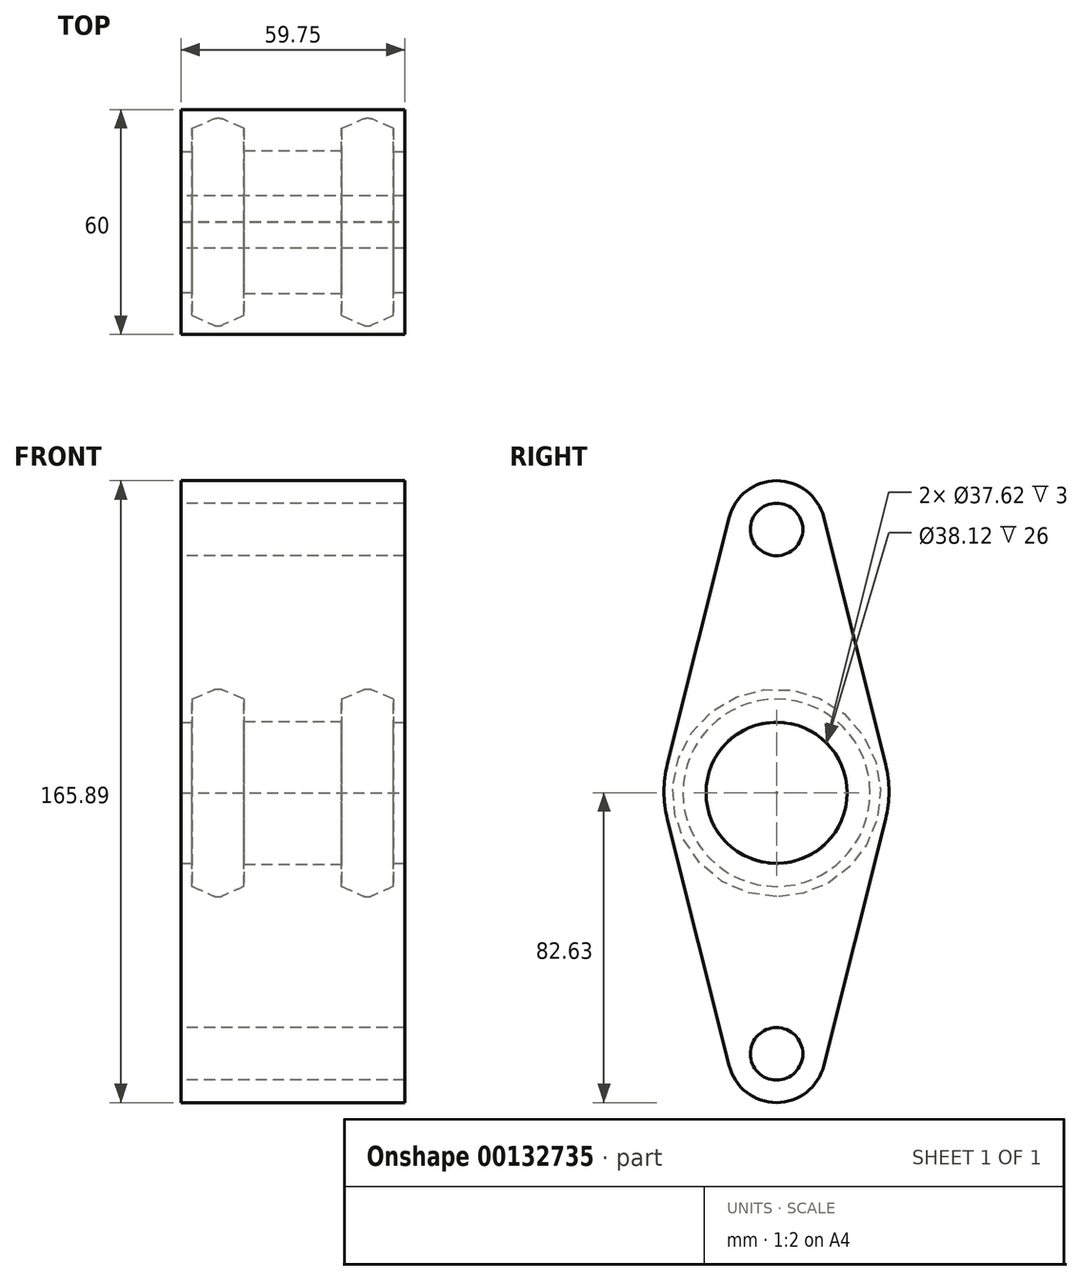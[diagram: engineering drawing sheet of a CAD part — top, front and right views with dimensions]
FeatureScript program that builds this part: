
annotation { "Feature Type Name" : "Feature", "Feature Type Description" : "" }
export const myFeature = defineFeature(function(context is Context, id is Id, definition is map)
    precondition{}
    {
        {
            var Q0;
            Q0=qCreatedBy(makeId("Front.planeOp"),FACE);
            var sketch = newSketch(context, id + "F0", { "sketchPlane" : qUnion([Q0])});
            skLineSegment(sketch, "E0", {"start": v(-26.44, 0) * mm, "end": v(-23.44, 0) * mm});
            skLineSegment(sketch, "E1", {"start": v(-23.44, 0) * mm, "end": v(-23.44, 6.15) * mm});
            skLineSegment(sketch, "E2", {"start": v(-23.44, 6.15) * mm, "end": v(-17.71, 8.67) * mm});
            skLineSegment(sketch, "E3", {"start": v(-11.46, 0) * mm, "end": v(-11.46, 0) * mm});
            skLineSegment(sketch, "E4", {"start": v(-9.57, 6.15) * mm, "end": v(-9.57, 0.25) * mm});
            skLineSegment(sketch, "E5", {"start": v(-9.57, 0.25) * mm, "end": v(3.43, 0.25) * mm});
            skLineSegment(sketch, "E6.MirrorCS", {"start": v(33.3, 0) * mm, "end": v(30.3, 0) * mm});
            skLineSegment(sketch, "E7.MirrorCS", {"start": v(30.3, 0) * mm, "end": v(30.3, 6.15) * mm});
            skLineSegment(sketch, "E8.MirrorCS", {"start": v(30.3, 6.15) * mm, "end": v(24.58, 8.67) * mm});
            skLineSegment(sketch, "E9.MirrorCS", {"start": v(22.16, 8.67) * mm, "end": v(16.43, 6.15) * mm});
            skLineSegment(sketch, "E10.MirrorCS", {"start": v(16.43, 6.15) * mm, "end": v(16.43, 0.25) * mm});
            skLineSegment(sketch, "E11.MirrorCS", {"start": v(16.43, 0.25) * mm, "end": v(3.43, 0.25) * mm});
            skLineSegment(sketch, "E12.MirrorCS", {"start": v(-23.44, -37.5) * mm, "end": v(-23.44, -43.65) * mm});
            skLineSegment(sketch, "E13.MirrorCS", {"start": v(-23.44, -43.65) * mm, "end": v(-17.71, -46.17) * mm});
            skLineSegment(sketch, "E14.MirrorCS", {"start": v(-15.3, -46.17) * mm, "end": v(-9.57, -43.65) * mm});
            skLineSegment(sketch, "E15.MirrorCS", {"start": v(-9.57, -43.65) * mm, "end": v(-9.57, -37.75) * mm});
            skLineSegment(sketch, "E16.MirrorCS", {"start": v(-9.57, -37.75) * mm, "end": v(3.43, -37.75) * mm});
            skLineSegment(sketch, "E17.MirrorCS", {"start": v(16.43, -37.75) * mm, "end": v(3.43, -37.75) * mm});
            skLineSegment(sketch, "E18.MirrorCS", {"start": v(16.43, -43.65) * mm, "end": v(16.43, -37.75) * mm});
            skLineSegment(sketch, "E19.MirrorCS", {"start": v(22.16, -46.17) * mm, "end": v(16.43, -43.65) * mm});
            skLineSegment(sketch, "E20.MirrorCS", {"start": v(30.3, -43.65) * mm, "end": v(24.58, -46.17) * mm});
            skLineSegment(sketch, "E21.MirrorCS", {"start": v(30.3, -37.5) * mm, "end": v(30.3, -43.65) * mm});
            skPoint(sketch, "E22.second.point", {"position": v(-16.45, 9.18) * mm});
            skPoint(sketch, "E22.third.point", {"position": v(-16.5, 4.16) * mm});
            skArc(sketch, "E23", {"start": v(-15.3, 8.67) * mm, "mid": v(-16.5, 8.93) * mm, "end": v(-17.71, 8.67) * mm});
            skArc(sketch, "E24.MirrorCS", {"start": v(-15.3, -46.17) * mm, "mid": v(-16.5, -46.43) * mm, "end": v(-17.71, -46.17) * mm});
            skArc(sketch, "E25.MirrorCS", {"start": v(22.16, 8.67) * mm, "mid": v(23.37, 8.93) * mm, "end": v(24.58, 8.67) * mm});
            skArc(sketch, "E26.MirrorCS", {"start": v(22.16, -46.17) * mm, "mid": v(23.37, -46.43) * mm, "end": v(24.58, -46.17) * mm});
            skLineSegment(sketch, "E27.trimOffspring", {"start": v(-15.3, 8.67) * mm, "end": v(-9.57, 6.15) * mm});
            skPoint(sketch, "E28.start.orphan", {"position": v(-16.5, 9.2) * mm});
            skPoint(sketch, "E29.orphan", {"position": v(23.37, 9.2) * mm});
            skPoint(sketch, "E30.orphan", {"position": v(23.37, -46.7) * mm});
            skPoint(sketch, "E31.orphan", {"position": v(-16.5, -46.7) * mm});
            skLineSegment(sketch, "E32", {"start": v(-26.44, -37.5) * mm, "end": v(-23.44, -37.5) * mm});
            skLineSegment(sketch, "E33", {"start": v(30.3, -37.5) * mm, "end": v(33.3, -37.5) * mm});
            skLineSegment(sketch, "E34", {"start": v(-26.44, 0) * mm, "end": v(-26.44, -18.75) * mm});
            skLineSegment(sketch, "E35", {"start": v(33.3, 0) * mm, "end": v(33.3, -18.75) * mm});
            skLineSegment(sketch, "E36", {"start": v(-26.44, -18.75) * mm, "end": v(33.3, -18.75) * mm});
            skSolve(sketch);
        }
        {
            var Q0;
            Q0=qCreatedBy(makeId("Front.planeOp"),FACE);
            var sketch = newSketch(context, id + "F1", { "sketchPlane" : qUnion([Q0])});
            skLineSegment(sketch, "E37", {"start": v(42.19, -18.81) * mm, "end": v(-37.88, -18.81) * mm});
            skSolve(sketch);
        }
        {
            var Q0;
            Q0=qCreatedBy(makeId("Right.planeOp"),FACE);
            var sketch = newSketch(context, id + "F2", { "sketchPlane" : qUnion([Q0])});
            skArc(sketch, "E38", {"start": v(-29.12, -11.19) * mm, "mid": v(-30.03, -18.5) * mm, "end": v(-29.12, -25.8) * mm});
            skPoint(sketch, "E39.0", {"position": v(0, -37.31) * mm});
            skArc(sketch, "E40", {"start": v(12.61, 54.6) * mm, "mid": v(0, 64.45) * mm, "end": v(-12.6, 54.62) * mm});
            skLineSegment(sketch, "E41", {"start": v(-29.12, -11.19) * mm, "end": v(-12.6, 54.62) * mm});
            skLineSegment(sketch, "E42", {"start": v(12.61, 54.6) * mm, "end": v(29.08, -11.21) * mm});
            skLineSegment(sketch, "E43", {"start": v(-33.72, -18.5) * mm, "end": v(35.57, -18.5) * mm});
            skCircle(sketch, "E44", {"center": v(0, 51.45) * mm, "radius": 7 * mm});
            skLineSegment(sketch, "E45.MirrorCS", {"start": v(-29.12, -25.8) * mm, "end": v(-12.6, -91.6) * mm});
            skArc(sketch, "E46.MirrorCS", {"start": v(12.61, -91.6) * mm, "mid": v(0, -101.44) * mm, "end": v(-12.6, -91.6) * mm});
            skLineSegment(sketch, "E47.MirrorCS", {"start": v(12.61, -91.6) * mm, "end": v(29.08, -25.77) * mm});
            skCircle(sketch, "E48.MirrorC", {"center": v(0, -88.44) * mm, "radius": 7 * mm});
            skArc(sketch, "E49.trimOffspring", {"start": v(29.08, -25.77) * mm, "mid": v(29.97, -18.5) * mm, "end": v(29.08, -11.21) * mm});
            skSolve(sketch);
        }
        {
            var Q0;
            Q0=makeQuery(id+"F0.imprint","IMPRINT",FACE,{"disambiguationData":[TD([[makeQuery(id+"F0.imprint","IMPRINT",EDGE,{"derivedFrom":sQuery(id+"F0.wireOp",EDGE,"E0")}),-1.0]])]});
            var Q1;
            Q1=sQuery(id+"F1.wireOp",EDGE,"E37");
            revolve(context, id + "F3", {"entities" : qUnion([Q0]), "axis" : qUnion([Q1]), "revolveType" : RevolveType.FULL});
        }
        {
            var Q0;
            Q0=makeQuery(id+"F2.imprint","IMPRINT",FACE,{"disambiguationData":[TD([[makeQuery(id+"F2.imprint","IMPRINT",EDGE,{"derivedFrom":sQuery(id+"F2.wireOp",EDGE,"E40")}),1.0]])]});
            var Q1;
            {var subQ0=sQuery(id+"F2.wireOp",EDGE,"E43");var subQ1=sQuery(id+"F2.wireOp",EDGE,"E38");var subQ2=makeQuery(id+"F2.imprint","INTERSECT",VERTEX,{"disambiguationData":[OD(0.0)],"derivedFrom":[subQ1,subQ0]});Q1=makeQuery(id+"F2.imprint","IMPRINT",FACE,{"disambiguationData":[TD([[makeQuery(id+"F2.imprint","IMPRINT",EDGE,{"disambiguationData":[TD([[subQ2,-1.0]])],"derivedFrom":subQ1}),1.0]])]});}
            var Q2;
            Q2=makeQuery(id+"F3.opRevolve","SWEPT_FACE",FACE,{"disambiguationData":[OSD([sQuery(id+"F0.wireOp",EDGE,"E35")])]});
            var Q3;
            Q3=makeQuery(id+"F3.opRevolve","SWEPT_FACE",FACE,{"disambiguationData":[OSD([sQuery(id+"F0.wireOp",EDGE,"E34")])]});
            extrude(context, id + "F4", {"entities" : qUnion([Q0, Q1]), "endBound" : BoundingType.UP_TO_SURFACE, "endBoundEntityFace" : qUnion([Q2]), "depth" : 25 * mm, "hasSecondDirection" : true, "secondDirectionBound" : SecondDirectionBoundingType.UP_TO_SURFACE, "secondDirectionOppositeDirection" : true, "secondDirectionBoundEntityFace" : qUnion([Q3]), "secondDirectionDepth" : 25 * mm});
        }
        {
            var Q0;
            Q0=makeQuery(id+"F3.opRevolve","SWEPT_BODY",BODY,{"disambiguationData":[OSD([sQuery(id+"F0.wireOp",EDGE,"E0"),sQuery(id+"F0.wireOp",EDGE,"E1"),sQuery(id+"F0.wireOp",EDGE,"E2"),sQuery(id+"F0.wireOp",EDGE,"E4"),sQuery(id+"F0.wireOp",EDGE,"E5"),sQuery(id+"F0.wireOp",EDGE,"E6.MirrorCS"),sQuery(id+"F0.wireOp",EDGE,"E7.MirrorCS"),sQuery(id+"F0.wireOp",EDGE,"E8.MirrorCS"),sQuery(id+"F0.wireOp",EDGE,"E9.MirrorCS"),sQuery(id+"F0.wireOp",EDGE,"E10.MirrorCS"),sQuery(id+"F0.wireOp",EDGE,"E11.MirrorCS"),sQuery(id+"F0.wireOp",EDGE,"E23"),sQuery(id+"F0.wireOp",EDGE,"E25.MirrorCS"),sQuery(id+"F0.wireOp",EDGE,"E27.trimOffspring"),sQuery(id+"F0.wireOp",EDGE,"E34"),sQuery(id+"F0.wireOp",EDGE,"E35"),sQuery(id+"F0.wireOp",EDGE,"E36")])]});
            var Q1;
            Q1=makeQuery(id+"F4.opExtrude","SWEPT_BODY",BODY,{"disambiguationData":[OSD([sQuery(id+"F2.wireOp",EDGE,"E38"),sQuery(id+"F2.wireOp",EDGE,"E40"),sQuery(id+"F2.wireOp",EDGE,"E41"),sQuery(id+"F2.wireOp",EDGE,"E42")])]});
            booleanBodies(context, id + "F5", {"operationType" : BooleanOperationType.SUBTRACTION, "tools" : qUnion([Q0]), "targets" : qUnion([Q1])});
        }
    });
